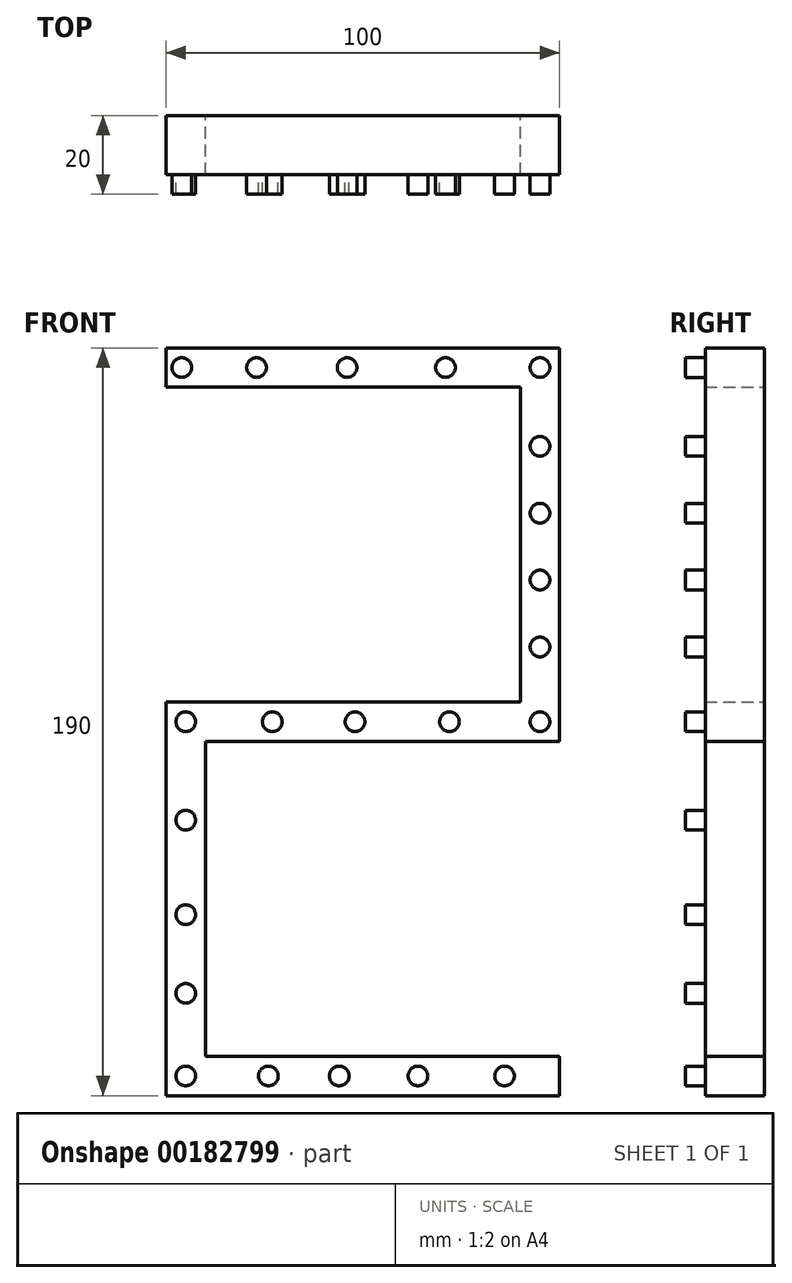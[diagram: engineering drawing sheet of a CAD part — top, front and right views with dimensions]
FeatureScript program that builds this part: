
annotation { "Feature Type Name" : "Feature", "Feature Type Description" : "" }
export const myFeature = defineFeature(function(context is Context, id is Id, definition is map)
    precondition{}
    {
        {
            var Q0;
            Q0=qCreatedBy(makeId("Front.planeOp"),FACE);
            var sketch = newSketch(context, id + "F0", { "sketchPlane" : qUnion([Q0])});
            skLineSegment(sketch, "E0", {"start": v(-100, 10) * mm, "end": v(-100, -90) * mm});
            skLineSegment(sketch, "E1", {"start": v(-100, -90) * mm, "end": v(0, -90) * mm});
            skLineSegment(sketch, "E2", {"start": v(0, -90) * mm, "end": v(0, -80) * mm});
            skLineSegment(sketch, "E3", {"start": v(0, -80) * mm, "end": v(-90, -80) * mm});
            skLineSegment(sketch, "E4", {"start": v(-90, -80) * mm, "end": v(-90, 0) * mm});
            skLineSegment(sketch, "E5", {"start": v(-100, 10) * mm, "end": v(-10, 10) * mm});
            skLineSegment(sketch, "E6", {"start": v(-90, 0) * mm, "end": v(0, 0) * mm});
            skLineSegment(sketch, "E7", {"start": v(0, 0) * mm, "end": v(0, 100) * mm});
            skLineSegment(sketch, "E8", {"start": v(0, 100) * mm, "end": v(-100, 100) * mm});
            skLineSegment(sketch, "E9", {"start": v(-100, 100) * mm, "end": v(-100, 90) * mm});
            skLineSegment(sketch, "E10", {"start": v(-100, 90) * mm, "end": v(-10, 90) * mm});
            skLineSegment(sketch, "E11", {"start": v(-10, 90) * mm, "end": v(-10, 10) * mm});
            skSolve(sketch);
        }
        {
            var Q0;
            Q0 = qSketchRegion(id + "F0", true);
            extrude(context, id + "F1", {"entities" : qUnion([Q0]), "depth" : 15 * mm});
        }
        {
            var Q0;
            Q0=makeQuery(id+"F1.opExtrude","CAP_FACE",FACE,{"disambiguationData":[OSD([sQuery(id+"F0.wireOp",EDGE,"E0"),sQuery(id+"F0.wireOp",EDGE,"E1"),sQuery(id+"F0.wireOp",EDGE,"E2"),sQuery(id+"F0.wireOp",EDGE,"E3"),sQuery(id+"F0.wireOp",EDGE,"E4"),sQuery(id+"F0.wireOp",EDGE,"E5"),sQuery(id+"F0.wireOp",EDGE,"E6"),sQuery(id+"F0.wireOp",EDGE,"E7"),sQuery(id+"F0.wireOp",EDGE,"E8"),sQuery(id+"F0.wireOp",EDGE,"E9"),sQuery(id+"F0.wireOp",EDGE,"E10"),sQuery(id+"F0.wireOp",EDGE,"E11")])],"isStart":false});
            var sketch = newSketch(context, id + "F2", { "sketchPlane" : qUnion([Q0])});
            skLineSegment(sketch, "E12", {"start": v(0, -85) * mm, "end": v(-95, -85) * mm, "construction": true});
            skLineSegment(sketch, "E13", {"start": v(-95, -85) * mm, "end": v(-95, 5) * mm, "construction": true});
            skLineSegment(sketch, "E14", {"start": v(-95, 5) * mm, "end": v(-5, 5) * mm, "construction": true});
            skLineSegment(sketch, "E15", {"start": v(-5, 5) * mm, "end": v(-5, 95) * mm, "construction": true});
            skLineSegment(sketch, "E16", {"start": v(-5, 95) * mm, "end": v(-100, 95) * mm, "construction": true});
            skCircle(sketch, "E17", {"center": v(-14, -85) * mm, "radius": 2.5 * mm});
            skCircle(sketch, "E18", {"center": v(-36, -85) * mm, "radius": 2.5 * mm});
            skCircle(sketch, "E19", {"center": v(-56, -85) * mm, "radius": 2.5 * mm});
            skCircle(sketch, "E20", {"center": v(-74, -85) * mm, "radius": 2.5 * mm});
            skCircle(sketch, "E21", {"center": v(-95, -85) * mm, "radius": 2.5 * mm});
            skCircle(sketch, "E22", {"center": v(-95, -64) * mm, "radius": 2.5 * mm});
            skCircle(sketch, "E23", {"center": v(-95, -44) * mm, "radius": 2.5 * mm});
            skCircle(sketch, "E24", {"center": v(-95, -20) * mm, "radius": 2.5 * mm});
            skCircle(sketch, "E25", {"center": v(-95, 5) * mm, "radius": 2.5 * mm});
            skCircle(sketch, "E26", {"center": v(-73, 5) * mm, "radius": 2.5 * mm});
            skCircle(sketch, "E27", {"center": v(-52, 5) * mm, "radius": 2.5 * mm});
            skCircle(sketch, "E28", {"center": v(-28, 5) * mm, "radius": 2.5 * mm});
            skCircle(sketch, "E29", {"center": v(-5, 5) * mm, "radius": 2.5 * mm});
            skCircle(sketch, "E30", {"center": v(-5, 24) * mm, "radius": 2.5 * mm});
            skCircle(sketch, "E31", {"center": v(-5, 41) * mm, "radius": 2.5 * mm});
            skCircle(sketch, "E32", {"center": v(-5, 58) * mm, "radius": 2.5 * mm});
            skCircle(sketch, "E33", {"center": v(-5, 75) * mm, "radius": 2.5 * mm});
            skCircle(sketch, "E34", {"center": v(-5, 95) * mm, "radius": 2.5 * mm});
            skCircle(sketch, "E35", {"center": v(-96, 95) * mm, "radius": 2.5 * mm});
            skCircle(sketch, "E36", {"center": v(-77, 95) * mm, "radius": 2.5 * mm});
            skCircle(sketch, "E37", {"center": v(-54, 95) * mm, "radius": 2.5 * mm});
            skCircle(sketch, "E38", {"center": v(-29, 95) * mm, "radius": 2.5 * mm});
            skSolve(sketch);
        }
        {
            var Q0;
            Q0 = qSketchRegion(id + "F2", true);
            extrude(context, id + "F3", {"entities" : qUnion([Q0]), "operationType" : NewBodyOperationType.ADD, "depth" : 5 * mm});
        }
    });
